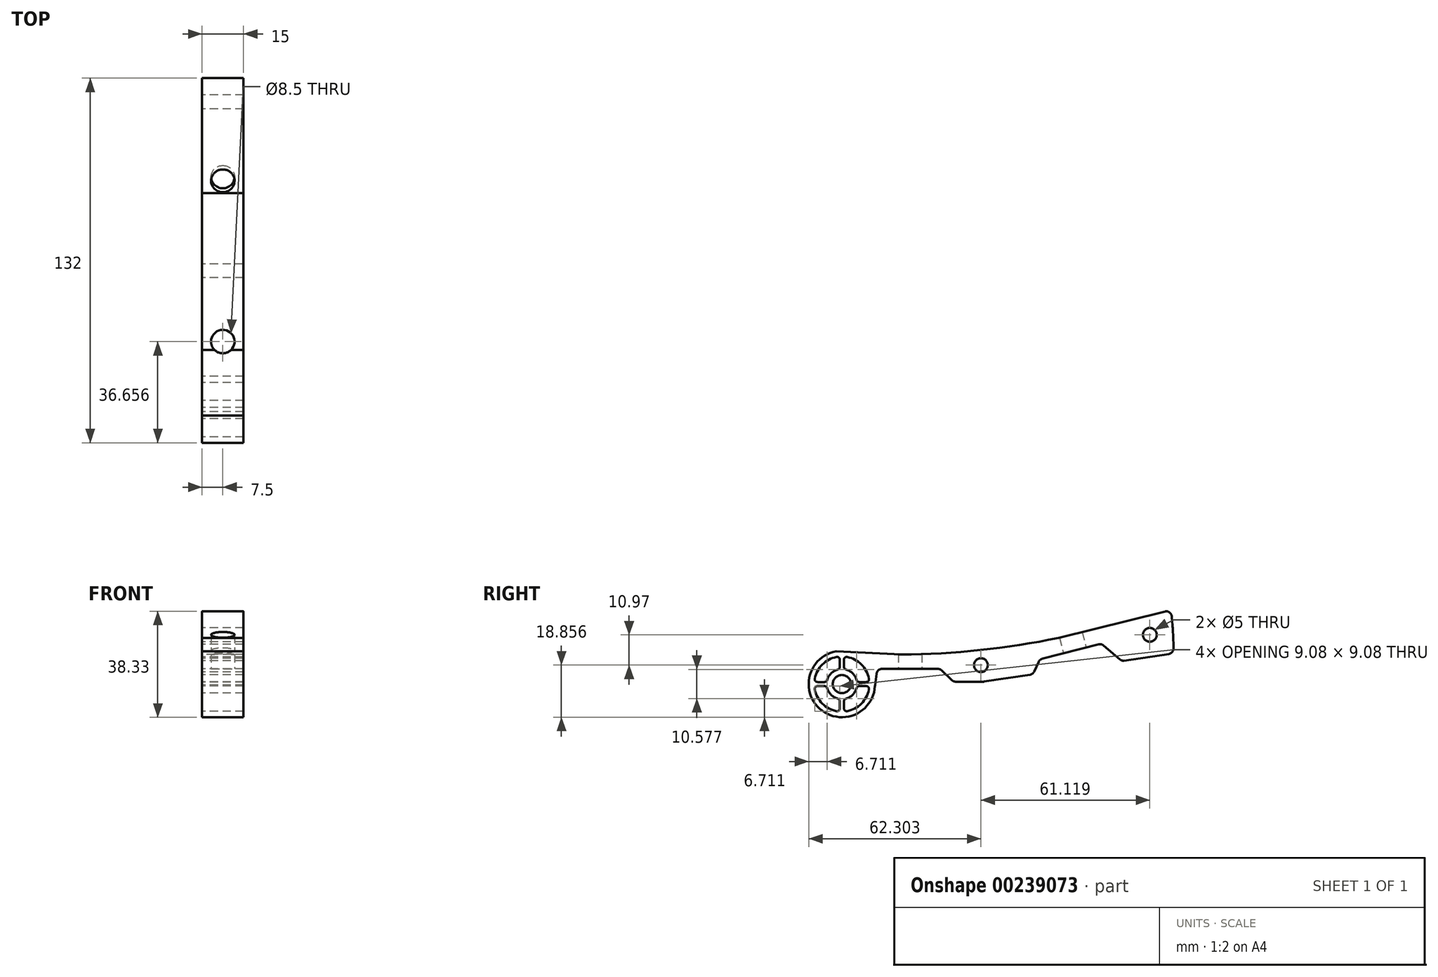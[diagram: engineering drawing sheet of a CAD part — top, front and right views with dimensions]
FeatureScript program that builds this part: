
annotation { "Feature Type Name" : "Feature", "Feature Type Description" : "" }
export const myFeature = defineFeature(function(context is Context, id is Id, definition is map)
    precondition{}
    {
        {
            var Q0;
            Q0=qCreatedBy(makeId("Right.planeOp"),FACE);
            var sketch = newSketch(context, id + "F0", { "sketchPlane" : qUnion([Q0])});
            skArc(sketch, "E0", {"start": v(21.96, 10.72) * mm, "mid": v(21.96, 10.73) * mm, "end": v(21.96, 10.73) * mm});
            skArc(sketch, "E1", {"start": v(120, 12.9) * mm, "mid": v(119.81, 18.73) * mm, "end": v(119.34, 24.54) * mm});
            skArc(sketch, "E2", {"start": v(21.46, 10.73) * mm, "mid": v(22.07, 10.72) * mm, "end": v(22.67, 10.8) * mm});
            skLineSegment(sketch, "E3", {"start": v(21.83, 10.72) * mm, "end": v(-2.06, 11.82) * mm});
            skLineSegment(sketch, "E4", {"start": v(78.34, 16.72) * mm, "end": v(116.87, 26.27) * mm});
            skCircle(sketch, "E5", {"center": v(0, 0) * mm, "radius": 3.3 * mm});
            skPoint(sketch, "E6.orphan", {"position": v(21.83, 9.28) * mm});
            skPoint(sketch, "E7.third.point", {"position": v(50.09, 12.3) * mm});
            skPoint(sketch, "E7.third.point.positionSnap0", {"position": v(50.09, 13.72) * mm});
            skArc(sketch, "E8", {"start": v(21.58, 10.73) * mm, "mid": v(50.11, 12.3) * mm, "end": v(78.34, 16.72) * mm});
            skCircle(sketch, "E9", {"center": v(111.42, 17.83) * mm, "radius": 2.5 * mm});
            skCircle(sketch, "E10", {"center": v(50.3, 6.86) * mm, "radius": 2.5 * mm});
            skArc(sketch, "E11", {"start": v(-2.06, 11.82) * mm, "mid": v(-7.99, -8.95) * mm, "end": v(11.98, -0.7) * mm});
            skLineSegment(sketch, "E12", {"start": v(118.3, 10.9) * mm, "end": v(102.16, 8.49) * mm});
            skLineSegment(sketch, "E13", {"start": v(51.16, 0.86) * mm, "end": v(41.18, 0.86) * mm});
            skPoint(sketch, "E14.visualSharp", {"position": v(11.97, 0.86) * mm});
            skArc(sketch, "E14.filletArc", {"start": v(12.07, -0.27) * mm, "mid": v(12, -0.48) * mm, "end": v(11.98, -0.7) * mm});
            skLineSegment(sketch, "E15", {"start": v(14.57, 5.48) * mm, "end": v(34.75, 5.48) * mm});
            skLineSegment(sketch, "E16", {"start": v(72.52, 9.15) * mm, "end": v(93, 14.35) * mm});
            skLineSegment(sketch, "E17", {"start": v(12.58, 3.74) * mm, "end": v(11.97, -1.01) * mm});
            skLineSegment(sketch, "E18", {"start": v(36.13, 4.93) * mm, "end": v(39.8, 1.42) * mm});
            skLineSegment(sketch, "E19", {"start": v(69.56, 4.51) * mm, "end": v(71.2, 8.05) * mm});
            skLineSegment(sketch, "E20", {"start": v(94.8, 13.92) * mm, "end": v(100.56, 8.95) * mm});
            skLineSegment(sketch, "E21.trimOffspring", {"start": v(68.04, 3.37) * mm, "end": v(51.45, 0.89) * mm});
            skPoint(sketch, "E22.visualSharp", {"position": v(119.08, 26.82) * mm});
            skArc(sketch, "E22.filletArc", {"start": v(119.34, 24.54) * mm, "mid": v(118.5, 25.97) * mm, "end": v(116.87, 26.27) * mm});
            skPoint(sketch, "E23.visualSharp", {"position": v(120, 11.16) * mm});
            skArc(sketch, "E23.filletArc", {"start": v(118.3, 10.9) * mm, "mid": v(119.52, 11.58) * mm, "end": v(120, 12.9) * mm});
            skPoint(sketch, "E24.visualSharp", {"position": v(101.25, 8.35) * mm});
            skArc(sketch, "E24.filletArc", {"start": v(100.56, 8.95) * mm, "mid": v(101.3, 8.54) * mm, "end": v(102.16, 8.49) * mm});
            skPoint(sketch, "E25.visualSharp", {"position": v(94.01, 14.6) * mm});
            skArc(sketch, "E25.filletArc", {"start": v(94.8, 13.92) * mm, "mid": v(93.95, 14.35) * mm, "end": v(93, 14.35) * mm});
            skPoint(sketch, "E26.visualSharp", {"position": v(71.6, 8.92) * mm});
            skArc(sketch, "E26.filletArc", {"start": v(72.52, 9.15) * mm, "mid": v(71.73, 8.75) * mm, "end": v(71.2, 8.05) * mm});
            skPoint(sketch, "E27.visualSharp", {"position": v(69.11, 3.53) * mm});
            skArc(sketch, "E27.filletArc", {"start": v(68.04, 3.37) * mm, "mid": v(68.95, 3.75) * mm, "end": v(69.56, 4.51) * mm});
            skPoint(sketch, "E28.visualSharp", {"position": v(40.38, 0.86) * mm});
            skArc(sketch, "E28.filletArc", {"start": v(39.8, 1.42) * mm, "mid": v(40.43, 1) * mm, "end": v(41.18, 0.86) * mm});
            skPoint(sketch, "E29.visualSharp", {"position": v(35.55, 5.48) * mm});
            skArc(sketch, "E29.filletArc", {"start": v(36.13, 4.93) * mm, "mid": v(35.5, 5.34) * mm, "end": v(34.75, 5.48) * mm});
            skPoint(sketch, "E30.visualSharp", {"position": v(12.8, 5.48) * mm});
            skArc(sketch, "E30.filletArc", {"start": v(14.57, 5.48) * mm, "mid": v(13.25, 4.99) * mm, "end": v(12.58, 3.74) * mm});
            skPoint(sketch, "E31.visualSharp", {"position": v(51.3, 0.86) * mm});
            skArc(sketch, "E31.filletArc", {"start": v(51.16, 0.86) * mm, "mid": v(51.3, 0.87) * mm, "end": v(51.45, 0.89) * mm});
            skArc(sketch, "E32", {"start": v(1.94, -9.8) * mm, "mid": v(7.07, -7.07) * mm, "end": v(9.8, -1.94) * mm});
            skArc(sketch, "E33", {"start": v(1.48, -5.3) * mm, "mid": v(3.89, -3.89) * mm, "end": v(5.3, -1.48) * mm});
            skArc(sketch, "E34", {"start": v(10.03, 0.75) * mm, "mid": v(10, 0.75) * mm, "end": v(9.97, 0.75) * mm});
            skLineSegment(sketch, "E35", {"start": v(-8.83, 0.75) * mm, "end": v(-6.26, 0.75) * mm});
            skLineSegment(sketch, "E36", {"start": v(-8.83, -0.75) * mm, "end": v(-6.26, -0.75) * mm});
            skLineSegment(sketch, "E37", {"start": v(-0.75, 8.83) * mm, "end": v(-0.75, 6.26) * mm});
            skLineSegment(sketch, "E38", {"start": v(0.75, 8.83) * mm, "end": v(0.75, 6.26) * mm});
            skPoint(sketch, "E39.center.orphan", {"position": v(0, -10) * mm});
            skPoint(sketch, "E40.center.orphan", {"position": v(0, 10) * mm});
            skArc(sketch, "E41.trimOffspring", {"start": v(-1.94, 9.8) * mm, "mid": v(-7.07, 7.07) * mm, "end": v(-9.8, 1.94) * mm});
            skPoint(sketch, "E42.center.orphan", {"position": v(-10, 0) * mm});
            skArc(sketch, "E43.trimOffspring", {"start": v(-9.8, -1.94) * mm, "mid": v(-7.07, -7.07) * mm, "end": v(-1.94, -9.8) * mm});
            skArc(sketch, "E44.trimOffspring", {"start": v(9.8, 1.94) * mm, "mid": v(7.07, 7.07) * mm, "end": v(1.94, 9.8) * mm});
            skLineSegment(sketch, "E45.trimOffspring", {"start": v(6.26, -0.75) * mm, "end": v(8.83, -0.75) * mm});
            skLineSegment(sketch, "E46.trimOffspring", {"start": v(6.26, 0.75) * mm, "end": v(8.83, 0.75) * mm});
            skLineSegment(sketch, "E47.trimOffspring", {"start": v(0.75, -6.26) * mm, "end": v(0.75, -8.83) * mm});
            skLineSegment(sketch, "E48.trimOffspring", {"start": v(-0.75, -6.26) * mm, "end": v(-0.75, -8.83) * mm});
            skArc(sketch, "E49.trimOffspring", {"start": v(5.3, 1.48) * mm, "mid": v(3.89, 3.89) * mm, "end": v(1.48, 5.3) * mm});
            skArc(sketch, "E50.trimOffspring", {"start": v(-1.48, 5.3) * mm, "mid": v(-3.89, 3.89) * mm, "end": v(-5.3, 1.48) * mm});
            skArc(sketch, "E51.trimOffspring", {"start": v(-5.3, -1.48) * mm, "mid": v(-3.89, -3.89) * mm, "end": v(-1.48, -5.3) * mm});
            skArc(sketch, "E52.filletArc", {"start": v(8.83, 0.75) * mm, "mid": v(9.6, 1.11) * mm, "end": v(9.8, 1.94) * mm});
            skPoint(sketch, "E53.visualSharp", {"position": v(0.75, 9.97) * mm});
            skArc(sketch, "E53.filletArc", {"start": v(1.94, 9.8) * mm, "mid": v(1.11, 9.6) * mm, "end": v(0.75, 8.83) * mm});
            skPoint(sketch, "E54.visualSharp", {"position": v(0.75, 5.45) * mm});
            skArc(sketch, "E54.filletArc", {"start": v(0.75, 6.26) * mm, "mid": v(0.95, 5.66) * mm, "end": v(1.48, 5.3) * mm});
            skPoint(sketch, "E55.visualSharp", {"position": v(5.45, 0.75) * mm});
            skArc(sketch, "E55.filletArc", {"start": v(5.3, 1.48) * mm, "mid": v(5.66, 0.95) * mm, "end": v(6.26, 0.75) * mm});
            skPoint(sketch, "E56.visualSharp", {"position": v(5.45, -0.75) * mm});
            skArc(sketch, "E56.filletArc", {"start": v(6.26, -0.75) * mm, "mid": v(5.66, -0.95) * mm, "end": v(5.3, -1.48) * mm});
            skPoint(sketch, "E57.visualSharp", {"position": v(9.97, -0.75) * mm});
            skArc(sketch, "E57.filletArc", {"start": v(9.8, -1.94) * mm, "mid": v(9.6, -1.11) * mm, "end": v(8.83, -0.75) * mm});
            skPoint(sketch, "E58.visualSharp", {"position": v(0.75, -5.45) * mm});
            skArc(sketch, "E58.filletArc", {"start": v(1.48, -5.3) * mm, "mid": v(0.95, -5.66) * mm, "end": v(0.75, -6.26) * mm});
            skPoint(sketch, "E59.visualSharp", {"position": v(0.75, -9.97) * mm});
            skArc(sketch, "E59.filletArc", {"start": v(0.75, -8.83) * mm, "mid": v(1.11, -9.6) * mm, "end": v(1.94, -9.8) * mm});
            skPoint(sketch, "E60.visualSharp", {"position": v(-0.75, -9.97) * mm});
            skArc(sketch, "E60.filletArc", {"start": v(-1.94, -9.8) * mm, "mid": v(-1.12, -9.6) * mm, "end": v(-0.75, -8.83) * mm});
            skPoint(sketch, "E61.visualSharp", {"position": v(-0.75, -5.45) * mm});
            skArc(sketch, "E61.filletArc", {"start": v(-0.75, -6.26) * mm, "mid": v(-0.95, -5.66) * mm, "end": v(-1.48, -5.3) * mm});
            skPoint(sketch, "E62.visualSharp", {"position": v(-5.45, -0.75) * mm});
            skArc(sketch, "E62.filletArc", {"start": v(-5.3, -1.48) * mm, "mid": v(-5.66, -0.95) * mm, "end": v(-6.26, -0.75) * mm});
            skPoint(sketch, "E63.visualSharp", {"position": v(-9.97, -0.75) * mm});
            skArc(sketch, "E63.filletArc", {"start": v(-8.83, -0.75) * mm, "mid": v(-9.6, -1.11) * mm, "end": v(-9.8, -1.94) * mm});
            skPoint(sketch, "E64.visualSharp", {"position": v(-9.97, 0.75) * mm});
            skArc(sketch, "E64.filletArc", {"start": v(-9.8, 1.94) * mm, "mid": v(-9.6, 1.11) * mm, "end": v(-8.83, 0.75) * mm});
            skPoint(sketch, "E65.visualSharp", {"position": v(-5.45, 0.75) * mm});
            skArc(sketch, "E65.filletArc", {"start": v(-6.26, 0.75) * mm, "mid": v(-5.66, 0.95) * mm, "end": v(-5.3, 1.48) * mm});
            skPoint(sketch, "E66.visualSharp", {"position": v(-0.75, 5.45) * mm});
            skArc(sketch, "E66.filletArc", {"start": v(-1.48, 5.3) * mm, "mid": v(-0.95, 5.66) * mm, "end": v(-0.75, 6.26) * mm});
            skPoint(sketch, "E67.visualSharp", {"position": v(-0.75, 9.97) * mm});
            skArc(sketch, "E67.filletArc", {"start": v(-0.75, 8.83) * mm, "mid": v(-1.11, 9.6) * mm, "end": v(-1.94, 9.8) * mm});
            skSolve(sketch);
        }
        {
            var Q0;
            {var subQ9=sQuery(id+"F0.wireOp",EDGE,"Z2RfFS8F-fJbA-lgiH-K7Vn-SxlDWFhEWRw2");Q0=makeQuery(id+"F0.imprint","IMPRINT",FACE,{"disambiguationData":[TD([[makeQuery(id+"F0.imprint","IMPRINT",EDGE,{"derivedFrom":subQ9}),-1.0]])]});}
            var Q1;
            Q1=qSketchRegion(id+"F0",true);
            extrude(context, id + "F1", {"entities" : qUnion([Q0, Q1]), "depth" : 15 * mm});
        }
        {
            var Q0;
            Q0=makeQuery(id+"F1.opExtrude","SWEPT_FACE",FACE,{"disambiguationData":[OSD([sQuery(id+"F0.wireOp",EDGE,"E15")])]});
            var sketch = newSketch(context, id + "F2", { "sketchPlane" : qUnion([Q0])});
            skCircle(sketch, "E68", {"center": v(7.5, -24.66) * mm, "radius": 4.25 * mm});
            skSolve(sketch);
        }
        {
            var Q0;
            Q0 = qSketchRegion(id + "F2", true);
            extrude(context, id + "F3", {"entities" : qUnion([Q0]), "operationType" : NewBodyOperationType.REMOVE, "oppositeDirection" : true, "depth" : 7.6 * mm});
        }
        {
            var Q0;
            Q0=makeQuery(id+"F1.opExtrude","SWEPT_FACE",FACE,{"disambiguationData":[OSD([sQuery(id+"F0.wireOp",EDGE,"E16")])]});
            var sketch = newSketch(context, id + "F4", { "sketchPlane" : qUnion([Q0])});
            skCircle(sketch, "E69", {"center": v(7.5, -84.67) * mm, "radius": 4.25 * mm});
            skSolve(sketch);
        }
        {
            var Q0;
            Q0 = qSketchRegion(id + "F4", true);
            extrude(context, id + "F5", {"entities" : qUnion([Q0]), "operationType" : NewBodyOperationType.REMOVE, "oppositeDirection" : true, "depth" : 15.8 * mm});
        }
    });
